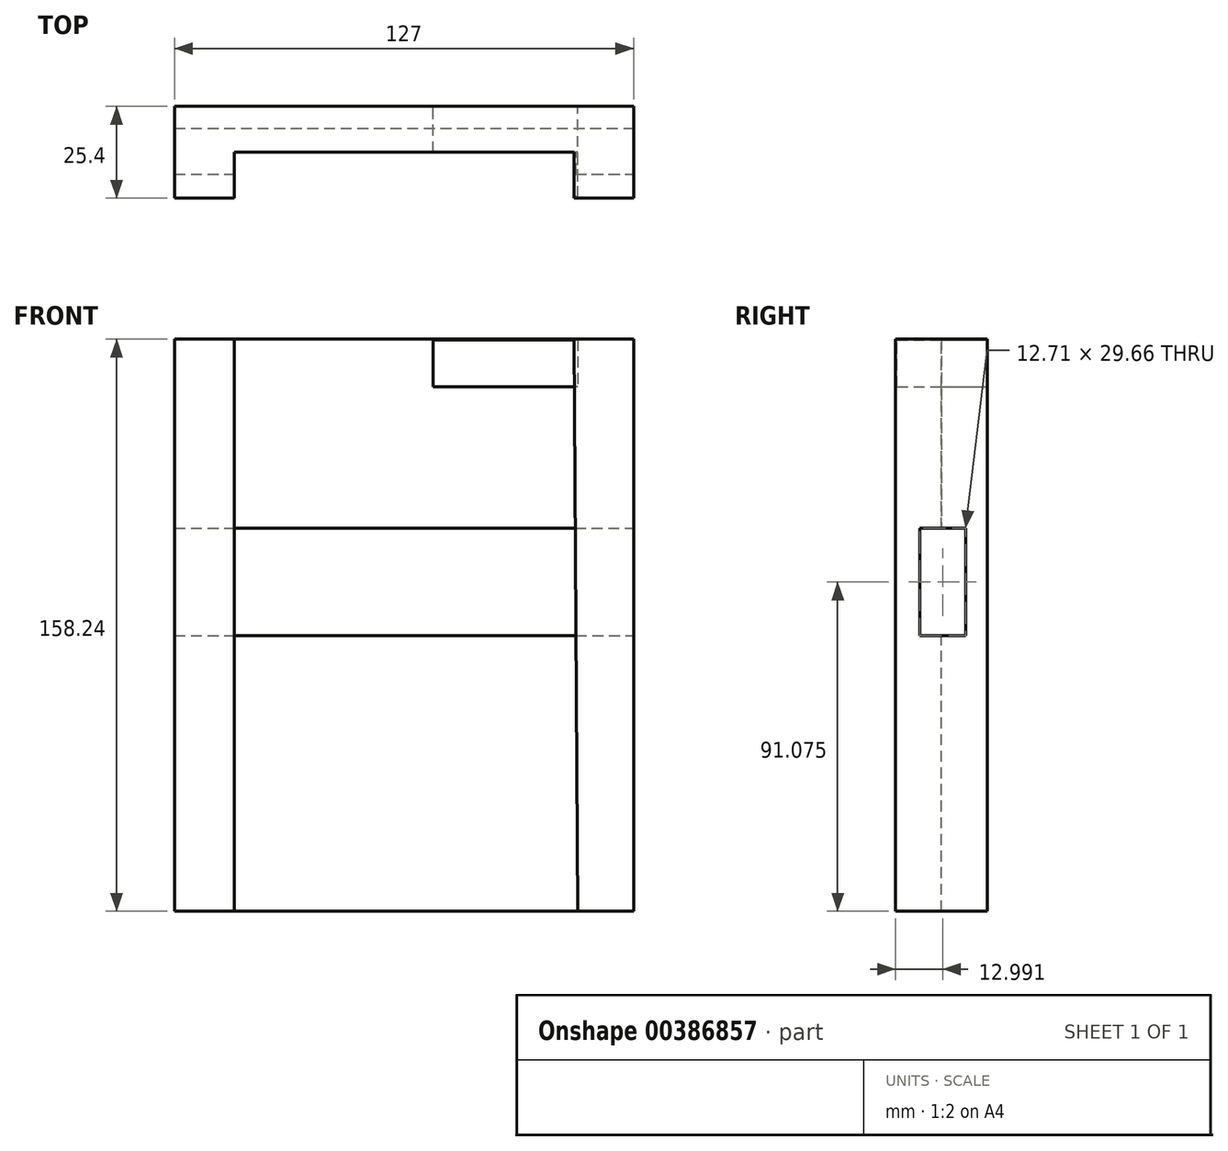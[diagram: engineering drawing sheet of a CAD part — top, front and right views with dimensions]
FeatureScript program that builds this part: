
annotation { "Feature Type Name" : "Feature", "Feature Type Description" : "" }
export const myFeature = defineFeature(function(context is Context, id is Id, definition is map)
    precondition{}
    {
        {
            var Q0;
            Q0=qCreatedBy(makeId("Front.planeOp"),FACE);
            var sketch = newSketch(context, id + "F0", { "sketchPlane" : qUnion([Q0])});
            skLineSegment(sketch, "E0.bottom", {"start": v(-63.5, 79.12) * mm, "end": v(63.5, 79.12) * mm});
            skLineSegment(sketch, "E0.top", {"start": v(-63.5, -79.12) * mm, "end": v(63.5, -79.12) * mm});
            skLineSegment(sketch, "E0.left", {"start": v(-63.5, 79.12) * mm, "end": v(-63.5, -79.12) * mm});
            skLineSegment(sketch, "E0.right", {"start": v(63.5, 79.12) * mm, "end": v(63.5, -79.12) * mm});
            skPoint(sketch, "E0.middle", {"position": v(0, 0) * mm});
            skSolve(sketch);
        }
        {
            var Q0;
            Q0 = qSketchRegion(id + "F0", true);
            extrude(context, id + "F1", {"entities" : qUnion([Q0]), "depth" : 25.4 * mm, "offsetDistance" : 25.4 * mm});
        }
        {
            var Q0;
            Q0=makeQuery(id+"F1.opExtrude","CAP_FACE",FACE,{"disambiguationData":[OSD([sQuery(id+"F0.wireOp",EDGE,"E0.bottom"),sQuery(id+"F0.wireOp",EDGE,"E0.top"),sQuery(id+"F0.wireOp",EDGE,"E0.left"),sQuery(id+"F0.wireOp",EDGE,"E0.right")])],"isStart":true});
            var sketch = newSketch(context, id + "F2", { "sketchPlane" : qUnion([Q0])});
            skSolve(sketch);
        }
        {
            var Q0;
            Q0=makeQuery(id+"F1.opExtrude","CAP_FACE",FACE,{"disambiguationData":[OSD([sQuery(id+"F0.wireOp",EDGE,"E0.bottom"),sQuery(id+"F0.wireOp",EDGE,"E0.top"),sQuery(id+"F0.wireOp",EDGE,"E0.left"),sQuery(id+"F0.wireOp",EDGE,"E0.right")])],"isStart":false});
            var sketch = newSketch(context, id + "F3", { "sketchPlane" : qUnion([Q0])});
            skLineSegment(sketch, "E1", {"start": v(46.9, 91.21) * mm, "end": v(-46.98, 91.21) * mm});
            skLineSegment(sketch, "E2", {"start": v(-46.98, 91.21) * mm, "end": v(-46.98, -86.59) * mm});
            skLineSegment(sketch, "E3", {"start": v(-46.98, -86.59) * mm, "end": v(48.08, -86.59) * mm});
            skLineSegment(sketch, "E4", {"start": v(48.08, -86.59) * mm, "end": v(46.9, 91.21) * mm});
            skSolve(sketch);
        }
        {
            var Q0;
            Q0 = qSketchRegion(id + "F3", true);
            extrude(context, id + "F4", {"entities" : qUnion([Q0]), "operationType" : NewBodyOperationType.REMOVE, "oppositeDirection" : true, "depth" : 12.7 * mm, "offsetDistance" : 25.4 * mm});
        }
        {
            var Q0;
            Q0=makeQuery(id+"F2.imprint","IMPRINT",FACE,{"disambiguationData":[TD([[makeQuery(id+"F2.imprint","IMPRINT",EDGE,{"derivedFrom":makeQuery(id+"F1.opExtrude","CAP_EDGE",EDGE,{"disambiguationData":[OSD([sQuery(id+"F0.wireOp",EDGE,"E0.bottom")])],"isStart":true})}),1.0]])]});
            var sketch = newSketch(context, id + "F5", { "sketchPlane" : qUnion([Q0])});
            skLineSegment(sketch, "E5.bottom", {"start": v(-48, 78.92) * mm, "end": v(-8, 78.92) * mm});
            skLineSegment(sketch, "E5.top", {"start": v(-48, 65.92) * mm, "end": v(-8, 65.92) * mm});
            skLineSegment(sketch, "E5.left", {"start": v(-48, 78.92) * mm, "end": v(-48, 65.92) * mm});
            skLineSegment(sketch, "E5.right", {"start": v(-8, 78.92) * mm, "end": v(-8, 65.92) * mm});
            skPoint(sketch, "E5.middle", {"position": v(-28, 72.42) * mm});
            skSolve(sketch);
        }
        {
            var Q0;
            Q0 = qSketchRegion(id + "F5", true);
            extrude(context, id + "F6", {"entities" : qUnion([Q0]), "operationType" : NewBodyOperationType.REMOVE, "oppositeDirection" : true, "depth" : 25 * mm, "offsetDistance" : 25 * mm});
        }
        {
            var Q0;
            Q0=makeQuery(id+"F1.opExtrude","SWEPT_FACE",FACE,{"disambiguationData":[OSD([sQuery(id+"F0.wireOp",EDGE,"E0.right")])]});
            var sketch = newSketch(context, id + "F7", { "sketchPlane" : qUnion([Q0])});
            skLineSegment(sketch, "E6.bottom", {"start": v(-18.76, 26.78) * mm, "end": v(-6.05, 26.78) * mm});
            skLineSegment(sketch, "E6.top", {"start": v(-18.76, -2.88) * mm, "end": v(-6.05, -2.88) * mm});
            skLineSegment(sketch, "E6.left", {"start": v(-18.76, 26.78) * mm, "end": v(-18.76, -2.88) * mm});
            skLineSegment(sketch, "E6.right", {"start": v(-6.05, 26.78) * mm, "end": v(-6.05, -2.88) * mm});
            skPoint(sketch, "E6.middle", {"position": v(-12.4, 11.95) * mm});
            skSolve(sketch);
        }
        {
            var Q0;
            Q0 = qSketchRegion(id + "F7", true);
            extrude(context, id + "F8", {"entities" : qUnion([Q0]), "operationType" : NewBodyOperationType.REMOVE, "oppositeDirection" : true, "depth" : 152.4 * mm, "offsetDistance" : 25.4 * mm});
        }
    });
